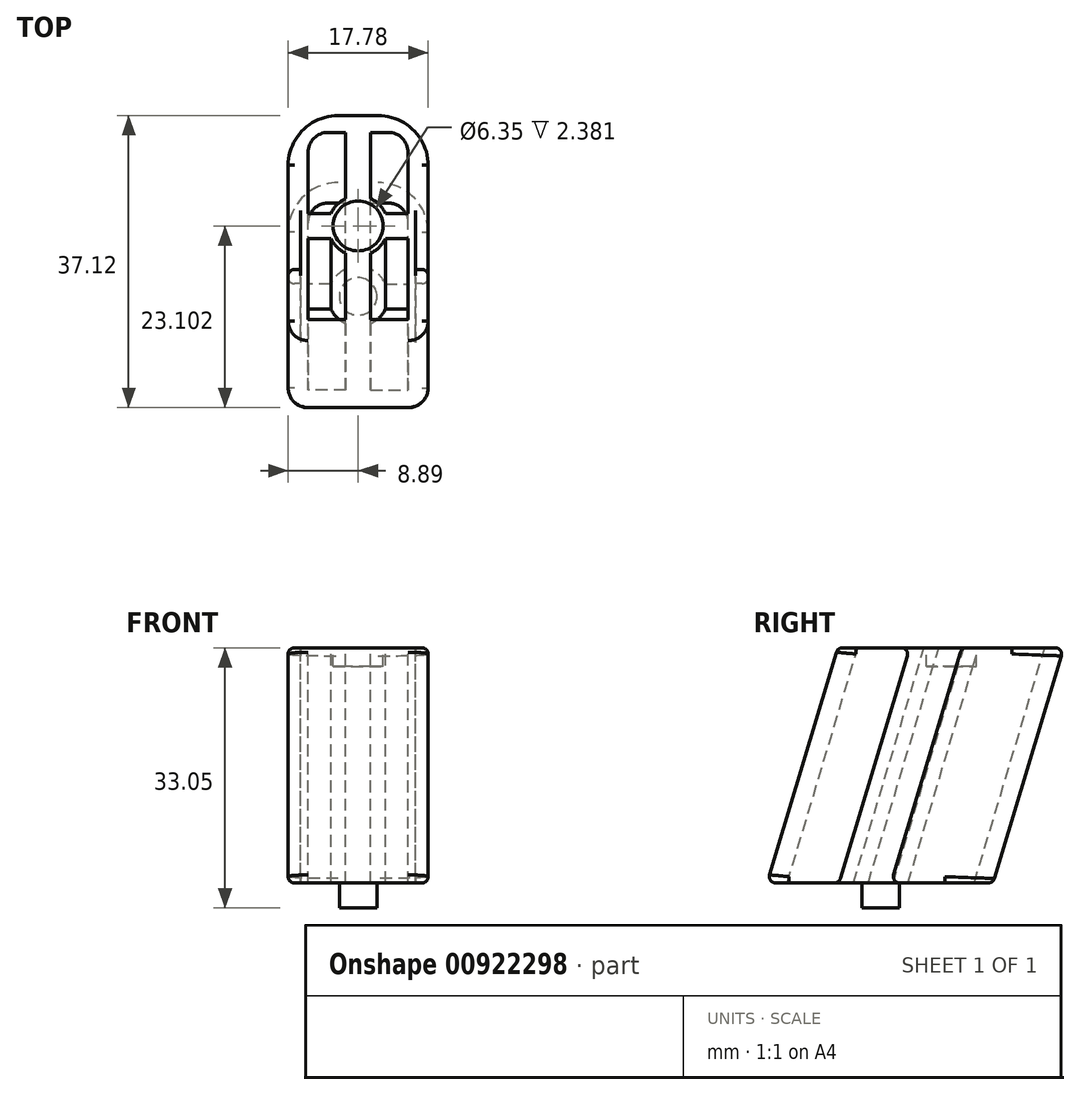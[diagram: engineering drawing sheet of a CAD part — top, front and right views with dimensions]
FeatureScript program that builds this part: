
annotation { "Feature Type Name" : "Feature", "Feature Type Description" : "" }
export const myFeature = defineFeature(function(context is Context, id is Id, definition is map)
    precondition{}
    {
        {
            var Q0;
            Q0=qCreatedBy(makeId("Top.planeOp"),FACE);
            var sketch = newSketch(context, id + "F0", { "sketchPlane" : qUnion([Q0])});
            skLineSegment(sketch, "E0", {"start": v(-6.35, -14.41) * mm, "end": v(6.35, -14.41) * mm});
            skLineSegment(sketch, "E1", {"start": v(8.9, -11.87) * mm, "end": v(8.9, -5.27) * mm});
            skLineSegment(sketch, "E2", {"start": v(2.54, 14.29) * mm, "end": v(-2.54, 14.29) * mm});
            skLineSegment(sketch, "E3", {"start": v(-8.9, 7.94) * mm, "end": v(-8.9, 1.33) * mm});
            skPoint(sketch, "E4.visualSharp", {"position": v(-8.9, 14.29) * mm});
            skArc(sketch, "E4.filletArc", {"start": v(-2.54, 14.29) * mm, "mid": v(-7.03, 12.43) * mm, "end": v(-8.9, 7.94) * mm});
            skPoint(sketch, "E5.visualSharp", {"position": v(8.9, 14.29) * mm});
            skArc(sketch, "E5.filletArc", {"start": v(8.9, 7.94) * mm, "mid": v(7.03, 12.43) * mm, "end": v(2.54, 14.29) * mm});
            skPoint(sketch, "E6.visualSharp", {"position": v(-8.89, -14.41) * mm});
            skArc(sketch, "E6.filletArc", {"start": v(-8.89, -11.87) * mm, "mid": v(-8.15, -13.67) * mm, "end": v(-6.35, -14.41) * mm});
            skPoint(sketch, "E7.visualSharp", {"position": v(8.9, -14.41) * mm});
            skArc(sketch, "E7.filletArc", {"start": v(6.35, -14.41) * mm, "mid": v(8.15, -13.67) * mm, "end": v(8.9, -11.87) * mm});
            skLineSegment(sketch, "E8", {"start": v(-8.89, 1.33) * mm, "end": v(-7.3, 1.33) * mm});
            skLineSegment(sketch, "E9", {"start": v(-7.3, 1.33) * mm, "end": v(-7.3, -5.27) * mm});
            skLineSegment(sketch, "E10", {"start": v(-7.3, -5.27) * mm, "end": v(-8.89, -5.27) * mm});
            skLineSegment(sketch, "E11.trimOffspring", {"start": v(-8.9, -5.27) * mm, "end": v(-8.9, -11.87) * mm});
            skLineSegment(sketch, "E12", {"start": v(8.9, 1.33) * mm, "end": v(7.3, 1.33) * mm});
            skLineSegment(sketch, "E13", {"start": v(7.3, 1.33) * mm, "end": v(7.3, -5.27) * mm});
            skLineSegment(sketch, "E14", {"start": v(7.3, -5.27) * mm, "end": v(8.9, -5.27) * mm});
            skLineSegment(sketch, "E15.trimOffspring", {"start": v(8.9, 1.33) * mm, "end": v(8.9, 7.94) * mm});
            skLineSegment(sketch, "E16", {"start": v(0, -14.41) * mm, "end": v(0, 14.29) * mm, "construction": true});
            skLineSegment(sketch, "E17", {"start": v(0, 0) * mm, "end": v(7.3, 0) * mm, "construction": true});
            skLineSegment(sketch, "E18.MirrorCS", {"start": v(0, 14.41) * mm, "end": v(0, -14.29) * mm, "construction": true});
            skLineSegment(sketch, "E19.MirrorCS", {"start": v(0, 0) * mm, "end": v(-7.3, 0) * mm, "construction": true});
            skLineSegment(sketch, "E20.bottom", {"start": v(-3.46, -1.59) * mm, "end": v(-6.35, -1.59) * mm});
            skLineSegment(sketch, "E20.top", {"start": v(-1.59, -11.87) * mm, "end": v(-6.35, -11.87) * mm});
            skLineSegment(sketch, "E20.left", {"start": v(-1.59, -3.46) * mm, "end": v(-1.59, -11.87) * mm});
            skLineSegment(sketch, "E20.right", {"start": v(-6.35, -1.59) * mm, "end": v(-6.35, -11.87) * mm});
            skLineSegment(sketch, "E21.MirrorCS", {"start": v(1.59, -11.87) * mm, "end": v(6.35, -11.87) * mm});
            skLineSegment(sketch, "E22.MirrorCS", {"start": v(6.35, -1.59) * mm, "end": v(6.35, -11.87) * mm});
            skLineSegment(sketch, "E23.MirrorCS", {"start": v(1.59, -3.46) * mm, "end": v(1.59, -11.87) * mm});
            skLineSegment(sketch, "E24.MirrorCS", {"start": v(3.46, -1.59) * mm, "end": v(6.35, -1.59) * mm});
            skLineSegment(sketch, "E25.MirrorCS", {"start": v(-3.46, 1.59) * mm, "end": v(-6.35, 1.59) * mm});
            skLineSegment(sketch, "E26.MirrorCS", {"start": v(3.46, 1.59) * mm, "end": v(6.35, 1.59) * mm});
            skLineSegment(sketch, "E27.MirrorCS", {"start": v(1.59, 3.46) * mm, "end": v(1.59, 11.87) * mm});
            skLineSegment(sketch, "E28.MirrorCS", {"start": v(-1.59, 3.46) * mm, "end": v(-1.59, 11.87) * mm});
            skLineSegment(sketch, "E29.MirrorCS", {"start": v(-6.35, 1.59) * mm, "end": v(-6.35, 9.33) * mm});
            skLineSegment(sketch, "E30.MirrorCS", {"start": v(6.35, 1.59) * mm, "end": v(6.35, 9.33) * mm});
            skLineSegment(sketch, "E31.MirrorCS", {"start": v(1.59, 11.87) * mm, "end": v(3.8, 11.87) * mm});
            skLineSegment(sketch, "E32.MirrorCS", {"start": v(-1.59, 11.87) * mm, "end": v(-3.81, 11.87) * mm});
            skArc(sketch, "E33", {"start": v(3.46, 1.59) * mm, "mid": v(2.7, 2.7) * mm, "end": v(1.59, 3.46) * mm});
            skPoint(sketch, "E34.orphan", {"position": v(1.59, 1.59) * mm});
            skPoint(sketch, "E35.orphan", {"position": v(-1.59, 1.59) * mm});
            skPoint(sketch, "E36.orphan", {"position": v(-1.59, -1.59) * mm});
            skPoint(sketch, "E37.orphan", {"position": v(1.59, -1.59) * mm});
            skArc(sketch, "E38.trimOffspring", {"start": v(-1.59, 3.46) * mm, "mid": v(-2.7, 2.7) * mm, "end": v(-3.46, 1.59) * mm});
            skArc(sketch, "E39.trimOffspring", {"start": v(-3.46, -1.59) * mm, "mid": v(-2.7, -2.7) * mm, "end": v(-1.59, -3.46) * mm});
            skArc(sketch, "E40.trimOffspring", {"start": v(1.59, -3.46) * mm, "mid": v(2.7, -2.7) * mm, "end": v(3.46, -1.59) * mm});
            skPoint(sketch, "E41.visualSharp", {"position": v(-6.35, 11.87) * mm});
            skArc(sketch, "E41.filletArc", {"start": v(-3.81, 11.87) * mm, "mid": v(-5.6, 11.13) * mm, "end": v(-6.35, 9.33) * mm});
            skPoint(sketch, "E42.visualSharp", {"position": v(6.35, 11.87) * mm});
            skArc(sketch, "E42.filletArc", {"start": v(6.35, 9.33) * mm, "mid": v(5.6, 11.13) * mm, "end": v(3.8, 11.87) * mm});
            skSolve(sketch);
        }
        {
            var Q0;
            Q0=qCreatedBy(makeId("Right.planeOp"),FACE);
            var sketch = newSketch(context, id + "F1", { "sketchPlane" : qUnion([Q0])});
            skLineSegment(sketch, "E43", {"start": v(0, 0) * mm, "end": v(8.96, 29.87) * mm});
            skLineSegment(sketch, "E44", {"start": v(0, 0) * mm, "end": v(15.25, 0) * mm, "construction": true});
            skSolve(sketch);
        }
        {
            var Q0;
            Q0 = qSketchRegion(id + "F0", true);
            var Q1;
            Q1=sQuery(id+"F1.wireOp",EDGE,"E43");
            sweep(context, id + "F2", {"profiles" : qUnion([Q0]), "path" : qUnion([Q1])});
        }
        {
            var Q0;
            Q0=makeQuery(id+"F0.imprint","IMPRINT",FACE,{"disambiguationData":[TD([[makeQuery(id+"F0.imprint","IMPRINT",EDGE,{"derivedFrom":sQuery(id+"F0.wireOp",EDGE,"E0")}),1.0]])]});
            var sketch = newSketch(context, id + "F3", { "sketchPlane" : qUnion([Q0])});
            skCircle(sketch, "E45", {"center": v(0, 0) * mm, "radius": 1.98 * mm});
            skSolve(sketch);
        }
        {
            var Q0;
            Q0 = qSketchRegion(id + "F3", true);
            extrude(context, id + "F4", {"entities" : qUnion([Q0]), "operationType" : NewBodyOperationType.ADD, "depth" : 2.38 * mm, "offsetDistance" : 25.4 * mm});
        }
        {
            var Q0;
            Q0=makeQuery(id+"F0.imprint","IMPRINT",FACE,{"disambiguationData":[TD([[makeQuery(id+"F0.imprint","IMPRINT",EDGE,{"derivedFrom":sQuery(id+"F0.wireOp",EDGE,"E0")}),1.0]])]});
            var sketch = newSketch(context, id + "F5", { "sketchPlane" : qUnion([Q0])});
            skCircle(sketch, "E46", {"center": v(0, 0) * mm, "radius": 2.38 * mm});
            skSolve(sketch);
        }
        {
            var Q0;
            Q0 = qSketchRegion(id + "F5", true);
            extrude(context, id + "F6", {"entities" : qUnion([Q0]), "oppositeDirection" : true, "depth" : 3.17 * mm, "offsetDistance" : 25.4 * mm});
        }
        {
            var Q0;
            Q0=makeQuery(id+"F2.opSweep","CAP_FACE",FACE,{"disambiguationData":[OSD([sQuery(id+"F0.wireOp",EDGE,"E0"),sQuery(id+"F0.wireOp",EDGE,"E1"),sQuery(id+"F0.wireOp",EDGE,"E2"),sQuery(id+"F0.wireOp",EDGE,"E3"),sQuery(id+"F0.wireOp",EDGE,"E4.filletArc"),sQuery(id+"F0.wireOp",EDGE,"E5.filletArc"),sQuery(id+"F0.wireOp",EDGE,"E6.filletArc"),sQuery(id+"F0.wireOp",EDGE,"E7.filletArc"),sQuery(id+"F0.wireOp",EDGE,"E8"),sQuery(id+"F0.wireOp",EDGE,"E9"),sQuery(id+"F0.wireOp",EDGE,"E10"),sQuery(id+"F0.wireOp",EDGE,"E11.trimOffspring"),sQuery(id+"F0.wireOp",EDGE,"E12"),sQuery(id+"F0.wireOp",EDGE,"E13"),sQuery(id+"F0.wireOp",EDGE,"E14"),sQuery(id+"F0.wireOp",EDGE,"E15.trimOffspring"),sQuery(id+"F0.wireOp",EDGE,"E20.bottom"),sQuery(id+"F0.wireOp",EDGE,"E20.top"),sQuery(id+"F0.wireOp",EDGE,"E20.left"),sQuery(id+"F0.wireOp",EDGE,"E20.right"),sQuery(id+"F0.wireOp",EDGE,"E21.MirrorCS"),sQuery(id+"F0.wireOp",EDGE,"E22.MirrorCS"),sQuery(id+"F0.wireOp",EDGE,"E23.MirrorCS"),sQuery(id+"F0.wireOp",EDGE,"E24.MirrorCS"),sQuery(id+"F0.wireOp",EDGE,"E25.MirrorCS"),sQuery(id+"F0.wireOp",EDGE,"E26.MirrorCS"),sQuery(id+"F0.wireOp",EDGE,"E27.MirrorCS"),sQuery(id+"F0.wireOp",EDGE,"E28.MirrorCS"),sQuery(id+"F0.wireOp",EDGE,"E29.MirrorCS"),sQuery(id+"F0.wireOp",EDGE,"E30.MirrorCS"),sQuery(id+"F0.wireOp",EDGE,"E31.MirrorCS"),sQuery(id+"F0.wireOp",EDGE,"E32.MirrorCS"),sQuery(id+"F1.wireOp",VERTEX,"E43.end")])],"isStart":false});
            var sketch = newSketch(context, id + "F7", { "sketchPlane" : qUnion([Q0])});
            skLineSegment(sketch, "E47", {"start": v(3.46, 10.55) * mm, "end": v(-3.46, 7.37) * mm, "construction": true});
            skCircle(sketch, "E48", {"center": v(0, 8.96) * mm, "radius": 3.18 * mm});
            skSolve(sketch);
        }
        {
            var Q0;
            Q0 = qSketchRegion(id + "F7", true);
            extrude(context, id + "F8", {"entities" : qUnion([Q0]), "operationType" : NewBodyOperationType.REMOVE, "oppositeDirection" : true, "depth" : 2.38 * mm, "offsetDistance" : 25.4 * mm});
        }
        {
            var Q0;
            Q0=makeQuery(id+"F2.opSweep","CAP_EDGE",EDGE,{"disambiguationData":[OSD([sQuery(id+"F0.wireOp",EDGE,"E5.filletArc"),sQuery(id+"F1.wireOp",VERTEX,"E43.start")])],"isStart":true});
            var Q1;
            Q1=makeQuery(id+"F2.opSweep","CAP_EDGE",EDGE,{"disambiguationData":[OSD([sQuery(id+"F0.wireOp",EDGE,"E1"),sQuery(id+"F1.wireOp",VERTEX,"E43.start")])],"isStart":true});
            var Q2;
            Q2=makeQuery(id+"F2.opSweep","CAP_EDGE",EDGE,{"disambiguationData":[OSD([sQuery(id+"F0.wireOp",EDGE,"E15.trimOffspring"),sQuery(id+"F1.wireOp",VERTEX,"E43.end")])],"isStart":false});
            var Q3;
            Q3=makeQuery(id+"F2.opSweep","CAP_EDGE",EDGE,{"disambiguationData":[OSD([sQuery(id+"F0.wireOp",EDGE,"E1"),sQuery(id+"F1.wireOp",VERTEX,"E43.end")])],"isStart":false});
            fillet(context, id + "F9", {"entities" : qUnion([Q0, Q1, Q2, Q3]), "radius" : 0.8 * mm, "tangentPropagation" : true, "allowEdgeOverflow" : false});
        }
        {
            var Q0;
            Q0=makeQuery(id+"F2.opSweep","SWEPT_EDGE",EDGE,{"disambiguationData":[OSD([sQuery(id+"F0.wireOp",EDGE,"E3"),sQuery(id+"F0.wireOp",EDGE,"E8"),sQuery(id+"F1.wireOp",EDGE,"E43")])]});
            var Q1;
            Q1=makeQuery(id+"F2.opSweep","SWEPT_EDGE",EDGE,{"disambiguationData":[OSD([sQuery(id+"F0.wireOp",EDGE,"E10"),sQuery(id+"F0.wireOp",EDGE,"E11.trimOffspring"),sQuery(id+"F1.wireOp",EDGE,"E43")])]});
            var Q2;
            Q2=makeQuery(id+"F2.opSweep","SWEPT_EDGE",EDGE,{"disambiguationData":[OSD([sQuery(id+"F0.wireOp",EDGE,"E1"),sQuery(id+"F0.wireOp",EDGE,"E14"),sQuery(id+"F1.wireOp",EDGE,"E43")])]});
            var Q3;
            Q3=makeQuery(id+"F2.opSweep","SWEPT_EDGE",EDGE,{"disambiguationData":[OSD([sQuery(id+"F0.wireOp",EDGE,"E12"),sQuery(id+"F0.wireOp",EDGE,"E15.trimOffspring"),sQuery(id+"F1.wireOp",EDGE,"E43")])]});
            fillet(context, id + "F10", {"entities" : qUnion([Q0, Q1, Q2, Q3]), "radius" : 0.8 * mm, "tangentPropagation" : true, "allowEdgeOverflow" : false});
        }
    });
